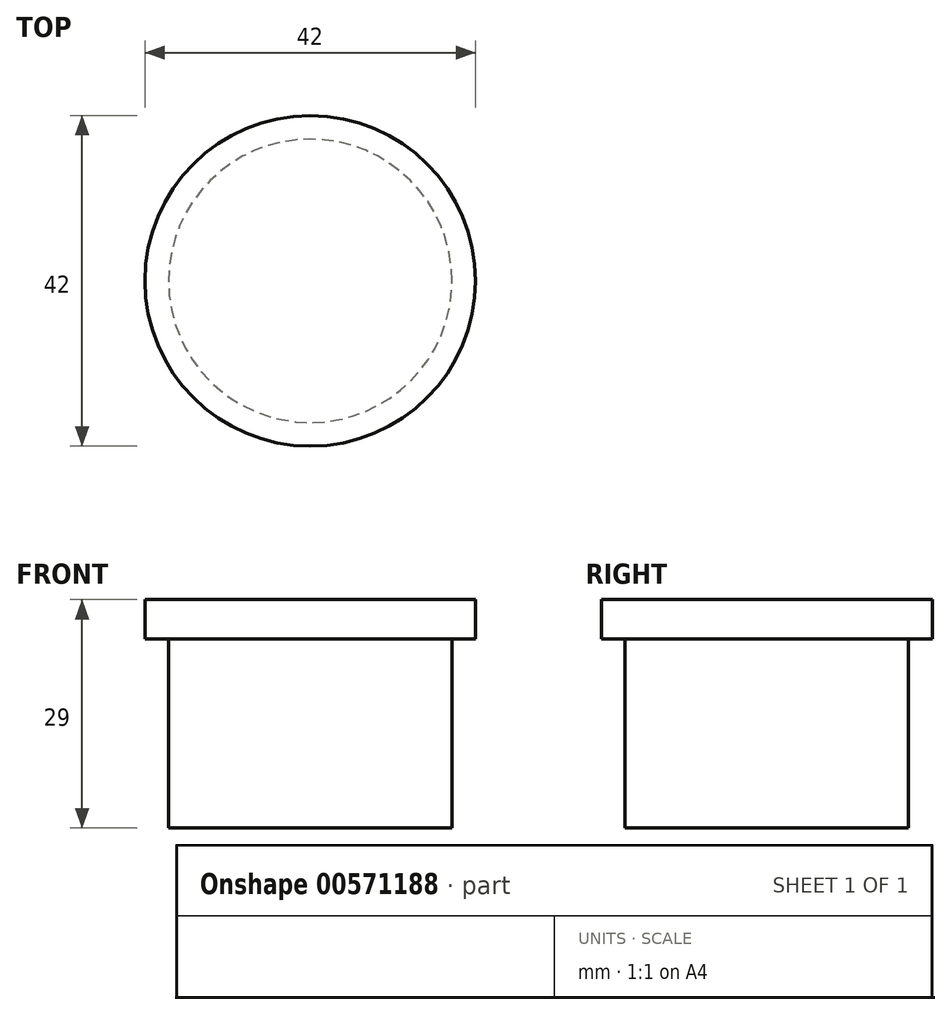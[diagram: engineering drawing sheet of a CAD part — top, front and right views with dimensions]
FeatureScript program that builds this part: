
annotation { "Feature Type Name" : "Feature", "Feature Type Description" : "" }
export const myFeature = defineFeature(function(context is Context, id is Id, definition is map)
    precondition{}
    {
        {
            var Q0;
            Q0=qCreatedBy(makeId("Front.planeOp"),FACE);
            var sketch = newSketch(context, id + "F0", { "sketchPlane" : qUnion([Q0])});
            skLineSegment(sketch, "E0", {"start": v(-21, 29) * mm, "end": v(-21, 24) * mm});
            skLineSegment(sketch, "E1", {"start": v(-21, 24) * mm, "end": v(-18, 24) * mm});
            skLineSegment(sketch, "E2", {"start": v(-18, 24) * mm, "end": v(-18, 0) * mm});
            skLineSegment(sketch, "E3", {"start": v(-18, 0) * mm, "end": v(0, 0) * mm});
            skLineSegment(sketch, "E4", {"start": v(0, 0) * mm, "end": v(0, 29) * mm});
            skLineSegment(sketch, "E5", {"start": v(0, 29) * mm, "end": v(-21, 29) * mm});
            skSolve(sketch);
        }
        {
            var Q0;
            Q0=sQuery(id+"F0.wireOp",EDGE,"E0");
            var Q1;
            Q1=sQuery(id+"F0.wireOp",EDGE,"E2");
            var Q2;
            Q2=sQuery(id+"F0.wireOp",EDGE,"E1");
            var Q3;
            Q3=sQuery(id+"F0.wireOp",EDGE,"E5");
            var Q4;
            Q4=sQuery(id+"F0.wireOp",EDGE,"E3");
            var Q5;
            Q5=sQuery(id+"F0.wireOp",EDGE,"E4");
            revolve(context, id + "F1", {"bodyType" : ToolBodyType.SURFACE, "surfaceEntities" : qUnion([Q0, Q1, Q2, Q3, Q4]), "axis" : qUnion([Q5]), "revolveType" : RevolveType.FULL});
        }
    });
